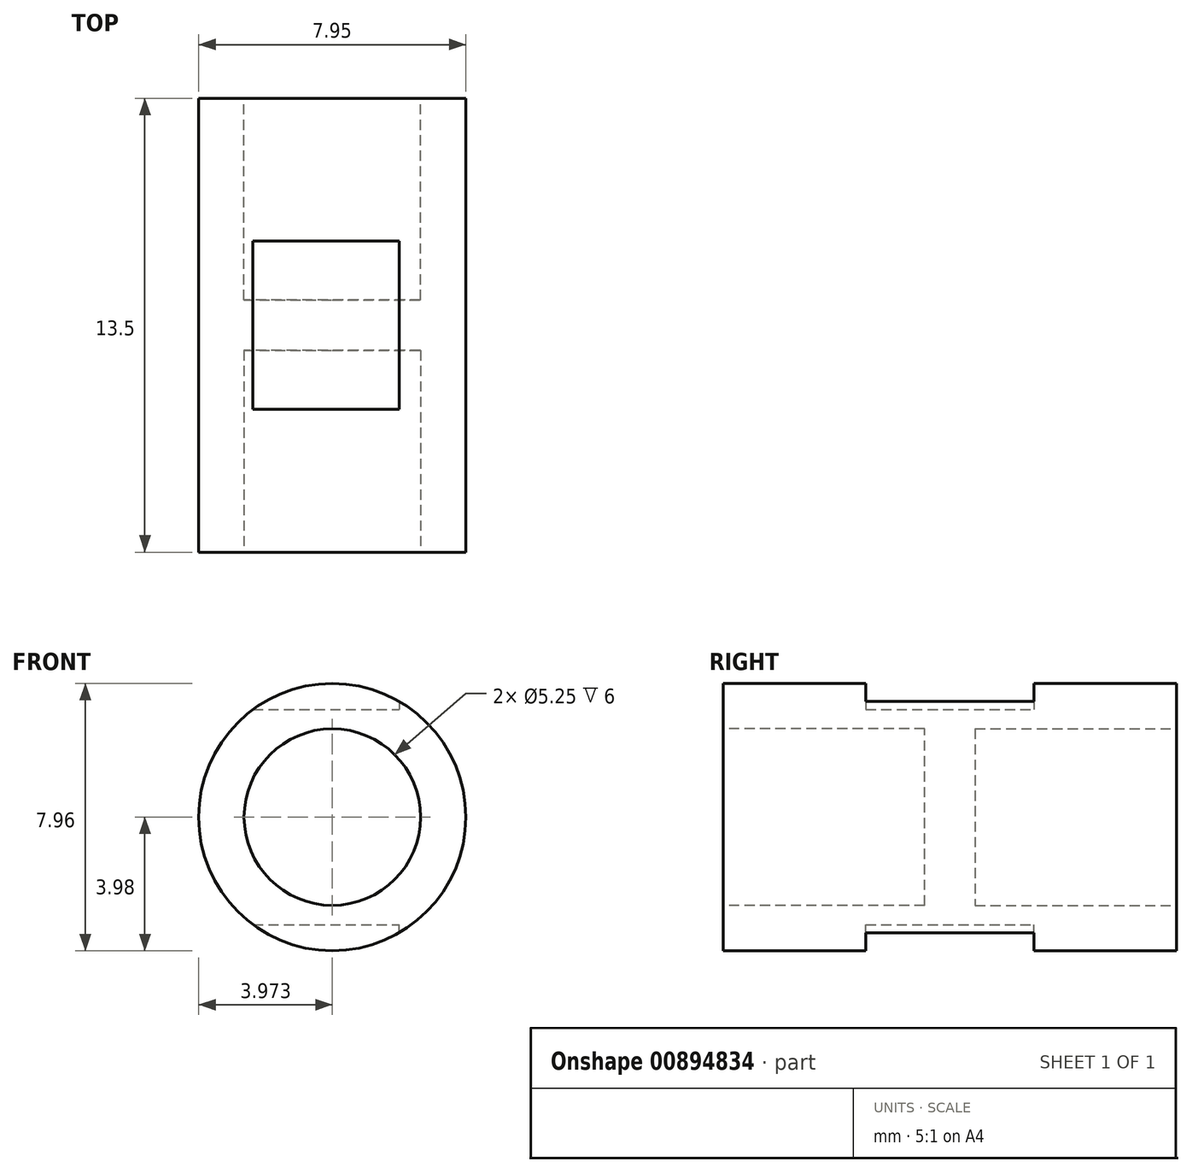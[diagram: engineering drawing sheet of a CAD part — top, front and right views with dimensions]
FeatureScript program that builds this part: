
annotation { "Feature Type Name" : "Feature", "Feature Type Description" : "" }
export const myFeature = defineFeature(function(context is Context, id is Id, definition is map)
    precondition{}
    {
        {
            var Q0;
            Q0=qCreatedBy(makeId("Top.planeOp"),FACE);
            var sketch = newSketch(context, id + "F0", { "sketchPlane" : qUnion([Q0])});
            skLineSegment(sketch, "E0.bottom", {"start": v(1.99, 6.75) * mm, "end": v(-1.99, 6.75) * mm});
            skLineSegment(sketch, "E0.top", {"start": v(1.99, -6.75) * mm, "end": v(-1.99, -6.75) * mm});
            skLineSegment(sketch, "E0.left", {"start": v(1.99, 6.75) * mm, "end": v(1.99, -6.75) * mm});
            skLineSegment(sketch, "E0.right", {"start": v(-1.99, 6.75) * mm, "end": v(-1.99, -6.75) * mm});
            skPoint(sketch, "E0.middle", {"position": v(0, 0) * mm});
            skSolve(sketch);
        }
        {
            var Q0;
            Q0=makeQuery(id+"F0.imprint","IMPRINT",FACE,{"disambiguationData":[TD([[makeQuery(id+"F0.imprint","IMPRINT",EDGE,{"derivedFrom":sQuery(id+"F0.wireOp",EDGE,"E0.bottom")}),1.0]])]});
            var Q1;
            Q1=sQuery(id+"F0.wireOp",EDGE,"E0.right");
            revolve(context, id + "F1", {"surfaceOperationType" : NewSurfaceOperationType.NEW, "entities" : qUnion([Q0]), "axis" : qUnion([Q1]), "revolveType" : RevolveType.FULL});
        }
        {
            var Q0;
            Q0=qCreatedBy(makeId("Right.planeOp"),FACE);
            var sketch = newSketch(context, id + "F2", { "sketchPlane" : qUnion([Q0])});
            skLineSegment(sketch, "E1.bottom", {"start": v(-2.5, -13.2) * mm, "end": v(2.5, -13.2) * mm});
            skLineSegment(sketch, "E1.top", {"start": v(-2.5, -3.2) * mm, "end": v(2.5, -3.2) * mm});
            skLineSegment(sketch, "E1.left", {"start": v(-2.5, -13.2) * mm, "end": v(-2.5, -3.2) * mm});
            skLineSegment(sketch, "E1.right", {"start": v(2.5, -13.2) * mm, "end": v(2.5, -3.2) * mm});
            skPoint(sketch, "E1.middle", {"position": v(0, -8.71) * mm});
            skPoint(sketch, "E2", {"position": v(0, -13.2) * mm});
            skLineSegment(sketch, "E3.bottom", {"start": v(2.5, 5.1) * mm, "end": v(-2.5, 5.1) * mm});
            skLineSegment(sketch, "E3.top", {"start": v(2.5, 3.2) * mm, "end": v(-2.5, 3.2) * mm});
            skLineSegment(sketch, "E3.left", {"start": v(2.5, 5.1) * mm, "end": v(2.5, 3.2) * mm});
            skLineSegment(sketch, "E3.right", {"start": v(-2.5, 5.1) * mm, "end": v(-2.5, 3.2) * mm});
            skPoint(sketch, "E3.middle", {"position": v(0, 4.15) * mm});
            skSolve(sketch);
        }
        {
            var Q0;
            Q0 = qSketchRegion(id + "F2", true);
            extrude(context, id + "F3", {"entities" : qUnion([Q0]), "operationType" : NewBodyOperationType.REMOVE, "oppositeDirection" : true, "depth" : 25 * mm, "offsetDistance" : 25 * mm});
        }
        {
            var Q0;
            Q0=makeQuery(id+"F1.opRevolve","SWEPT_FACE",FACE,{"disambiguationData":[OSD([sQuery(id+"F0.wireOp",EDGE,"E0.top")])]});
            var sketch = newSketch(context, id + "F4", { "sketchPlane" : qUnion([Q0])});
            skCircle(sketch, "E4", {"center": v(-1.99, 0) * mm, "radius": 2.62 * mm});
            skSolve(sketch);
        }
        {
            var Q0;
            Q0 = qSketchRegion(id + "F4", true);
            extrude(context, id + "F5", {"entities" : qUnion([Q0]), "operationType" : NewBodyOperationType.REMOVE, "oppositeDirection" : true, "depth" : 6 * mm, "offsetDistance" : 25 * mm});
        }
        {
            var Q0;
            Q0=makeQuery(id+"F1.opRevolve","SWEPT_FACE",FACE,{"disambiguationData":[OSD([sQuery(id+"F0.wireOp",EDGE,"E0.bottom")])]});
            var sketch = newSketch(context, id + "F6", { "sketchPlane" : qUnion([Q0])});
            skCircle(sketch, "E5", {"center": v(1.99, 0) * mm, "radius": 2.62 * mm});
            skSolve(sketch);
        }
        {
            var Q0;
            Q0 = qSketchRegion(id + "F6", true);
            extrude(context, id + "F7", {"entities" : qUnion([Q0]), "operationType" : NewBodyOperationType.REMOVE, "oppositeDirection" : true, "depth" : 6 * mm, "offsetDistance" : 25 * mm});
        }
    });
